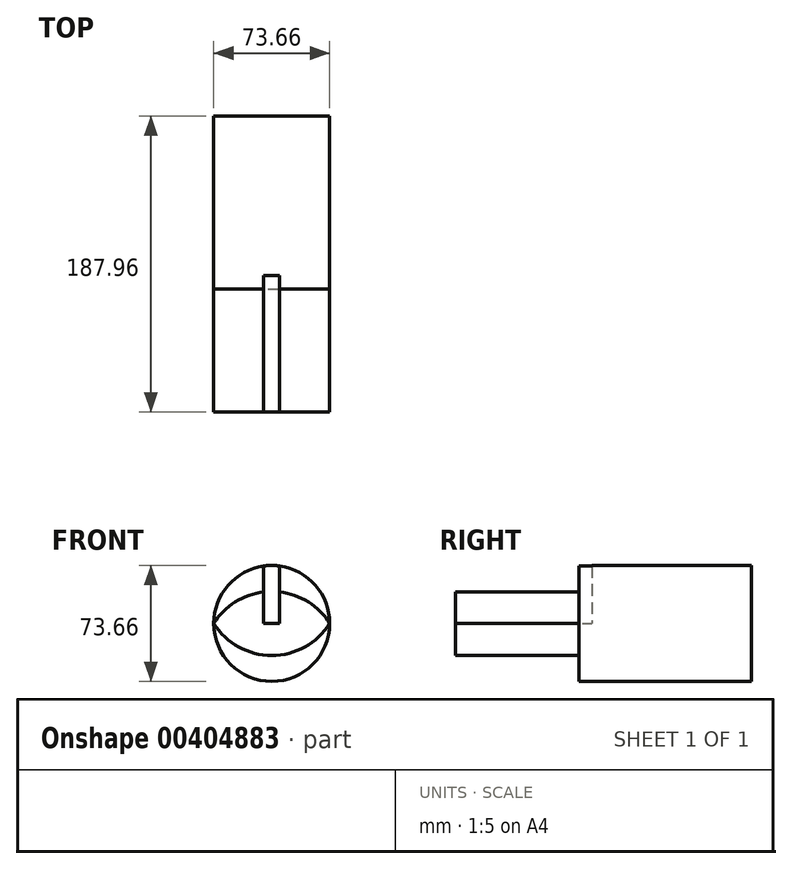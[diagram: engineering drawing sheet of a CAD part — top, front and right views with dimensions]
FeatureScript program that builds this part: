
annotation { "Feature Type Name" : "Feature", "Feature Type Description" : "" }
export const myFeature = defineFeature(function(context is Context, id is Id, definition is map)
    precondition{}
    {
        {
            var Q0;
            Q0=qCreatedBy(makeId("Front.planeOp"),FACE);
            var sketch = newSketch(context, id + "F0", { "sketchPlane" : qUnion([Q0])});
            skCircle(sketch, "E0", {"center": v(0, 0) * mm, "radius": 36.83 * mm});
            skSolve(sketch);
        }
        {
            var Q0;
            Q0 = qSketchRegion(id + "F0", true);
            extrude(context, id + "F1", {"entities" : qUnion([Q0]), "depth" : 109.73 * mm});
        }
        {
            var Q0;
            Q0=makeQuery(id+"F1.opExtrude","CAP_FACE",FACE,{"disambiguationData":[OSD([sQuery(id+"F0.wireOp",EDGE,"E0")])],"isStart":false});
            var sketch = newSketch(context, id + "F2", { "sketchPlane" : qUnion([Q0])});
            skArc(sketch, "E1", {"start": v(36.83, 0) * mm, "mid": v(0, 20.35) * mm, "end": v(-36.83, 0) * mm});
            skLineSegment(sketch, "E2", {"start": v(-36.83, 0) * mm, "end": v(3.18, 0) * mm});
            skArc(sketch, "E3.MirrorCS", {"start": v(36.83, 0) * mm, "mid": v(0, -20.35) * mm, "end": v(-36.83, 0) * mm});
            skSolve(sketch);
        }
        {
            var Q0;
            Q0 = qSketchRegion(id + "F2", true);
            extrude(context, id + "F3", {"entities" : qUnion([Q0]), "operationType" : NewBodyOperationType.ADD, "depth" : 78.23 * mm});
        }
        {
            var Q0;
            Q0=qCreatedBy(makeId("Top.planeOp"),FACE);
            var sketch = newSketch(context, id + "F4", { "sketchPlane" : qUnion([Q0])});
            skLineSegment(sketch, "E4", {"start": v(0, -105.25) * mm, "end": v(0, -204.63) * mm});
            skLineSegment(sketch, "E5.bottom", {"start": v(-5.08, -189.8) * mm, "end": v(5.08, -189.8) * mm});
            skLineSegment(sketch, "E5.top", {"start": v(-5.08, -101.3) * mm, "end": v(5.08, -101.3) * mm});
            skLineSegment(sketch, "E5.left", {"start": v(-5.08, -189.8) * mm, "end": v(-5.08, -101.3) * mm});
            skLineSegment(sketch, "E5.right", {"start": v(5.08, -189.8) * mm, "end": v(5.08, -101.3) * mm});
            skPoint(sketch, "E5.middle", {"position": v(0, -145.55) * mm});
            skSolve(sketch);
        }
        {
            var Q0;
            Q0 = qSketchRegion(id + "F4", true);
            extrude(context, id + "F5", {"entities" : qUnion([Q0]), "operationType" : NewBodyOperationType.REMOVE, "endBound" : BoundingType.THROUGH_ALL, "depth" : 25.4 * mm});
        }
    });
